# Revit family: zzzWater_Heater-Mini_Tank-Chronomite-CMT_Series
name_source: partatom
category: Plumbing Fixtures
units: mm (PartAtom-declared; Revit-internal decimal feet)

## family parameters
Cut with Voids When Loaded = No
Host = Face
OmniClass Number = 23.65.35.11.14
OmniClass Title = Instantaneous Water Heaters
Part Type = Normal
Room Calculation Point = No
Round Connector Dimension = Use Diameter
Shared = Yes

## types (4) — shared parameters
Assembly Code = D2020200
CMT - ST70 (150°F) Tempering Valve = No
CW Connection = Yes
Cold Water Connection Diameter = 1/2"
Corner R = 3/4"
Country = U.S.A.
D = 4"
Default Elevation = 0"
Description = CMT Series - Mini Tank Water Heater
E = 6"
Electrical Current = 12 A
Federal Public Law 111-360 (No Lead) = Yes
Finish = Stainless Steel-Chronomite-White
Finish- CW Indicator = Plastic-Chronomite-Blue
Finish- HW Indicator = Plastic-Chronomite-Red
H = 2 1/2"
HW Connection = Yes
Heating Capacity = 1440 watts
Hot Water Connection Diameter = 1/2"
Installation Instruction Link = https://www.chronomite.com
Installation Type = Wall Mounted
Manufacturer = Chronomite
Material = Stainless Steel-Chronomite-White
Maximum Operating Pressure = 80 PSI
Maximum Pressure = 150 PSI
Price = Prices may vary. Please consult Manufacturer Representative for most up-to-date price list.
Product Documentation Link = https://www.chronomite.com
Product Page URL = https://www.chronomite.com
Temperature Range = 50°-140°F
URL = https://www.chronomite.com
Vent Connection = No
Voltage = 110/120 Volts
Waste Connection = No
cULus Listed = Yes
zero-valued in all types: CWFU, HWFU, WFU

## per-type parameters (varying)
| type | A | B | C- Width | C/2 | Capacity (Gallons) | F | G- Height | G/2 | Weight Lbs |
| CMT-1.3 | 10" | 2 1/4" | 11" | 5 1/2" | 1.3 CF | 13 1/2" | 12 1/2" | 6 1/4" | 15 lbs. |
| CMT-2.5 | 10 3/8" | 2 3/4" | 11 3/4" | 5 7/8" | 2.5 CF | 15 1/2" | 14 1/2" | 7 1/4" | 18 lbs. |
| CMT-4.0 | 10 3/8" | 2 3/4" | 11 3/4" | 5 7/8" | 4 CF | 20 1/4" | 19 1/4" | 9 5/8" | 22 lbs |
| CMT-6.0 | 15 1/2" | 2 3/4" | 15 3/4" | 7 7/8" | 6 CF | 19" | 18" | 9" | 26 lbs. |

note: column(s) folded — value = type name in every type: Model

## geometry (parser evidence)
native form markers: Sweep x2
no freeform markers — native parametric forms only
